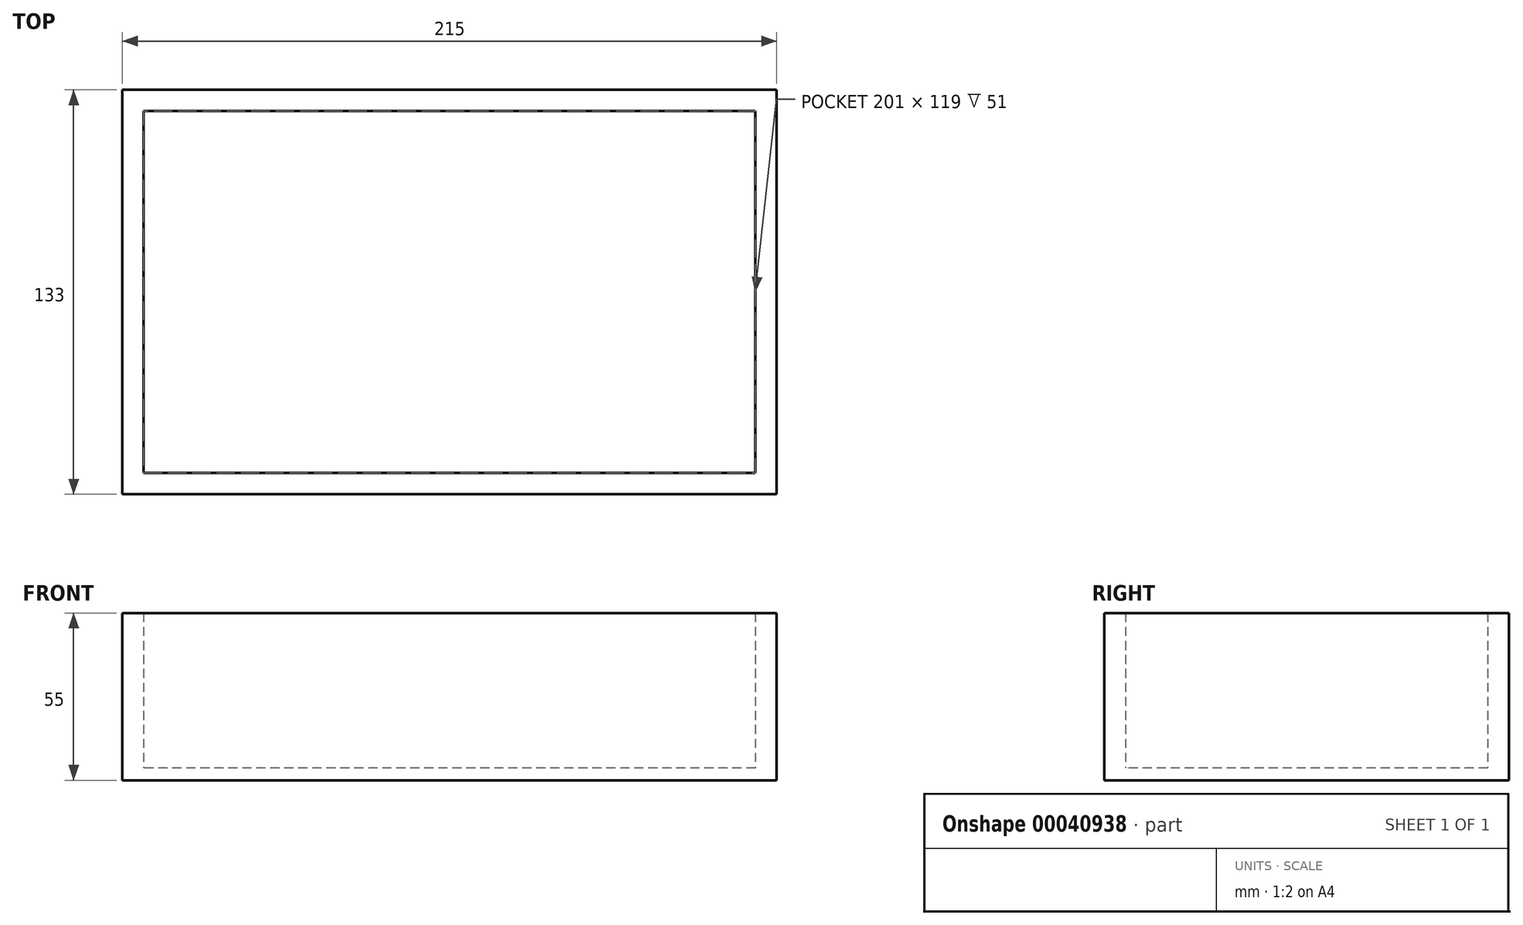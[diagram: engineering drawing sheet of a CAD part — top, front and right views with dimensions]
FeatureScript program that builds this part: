
annotation { "Feature Type Name" : "Feature", "Feature Type Description" : "" }
export const myFeature = defineFeature(function(context is Context, id is Id, definition is map)
    precondition{}
    {
        {
            var Q0;
            Q0=qCreatedBy(makeId("Top.planeOp"),FACE);
            var sketch = newSketch(context, id + "F0", { "sketchPlane" : qUnion([Q0])});
            skLineSegment(sketch, "E0.bottom", {"start": v(-99.18, 98.24) * mm, "end": v(115.82, 98.24) * mm});
            skLineSegment(sketch, "E0.top", {"start": v(-99.18, -34.76) * mm, "end": v(115.82, -34.76) * mm});
            skLineSegment(sketch, "E0.left", {"start": v(-99.18, 98.24) * mm, "end": v(-99.18, -34.76) * mm});
            skLineSegment(sketch, "E0.right", {"start": v(115.82, 98.24) * mm, "end": v(115.82, -34.76) * mm});
            skLineSegment(sketch, "E1.bottom", {"start": v(-99.18, -34.76) * mm, "end": v(-92.18, -34.76) * mm, "construction": true});
            skLineSegment(sketch, "E1.top", {"start": v(-99.18, -27.76) * mm, "end": v(-92.18, -27.76) * mm, "construction": true});
            skLineSegment(sketch, "E1.left", {"start": v(-99.18, -34.76) * mm, "end": v(-99.18, -27.76) * mm, "construction": true});
            skLineSegment(sketch, "E1.right", {"start": v(-92.18, -34.76) * mm, "end": v(-92.18, -27.76) * mm, "construction": true});
            skLineSegment(sketch, "E2.bottom", {"start": v(115.82, 98.24) * mm, "end": v(108.82, 98.24) * mm, "construction": true});
            skLineSegment(sketch, "E2.top", {"start": v(115.82, 91.24) * mm, "end": v(108.82, 91.24) * mm, "construction": true});
            skLineSegment(sketch, "E2.left", {"start": v(115.82, 98.24) * mm, "end": v(115.82, 91.24) * mm, "construction": true});
            skLineSegment(sketch, "E2.right", {"start": v(108.82, 98.24) * mm, "end": v(108.82, 91.24) * mm, "construction": true});
            skLineSegment(sketch, "E3.bottom", {"start": v(108.82, 91.24) * mm, "end": v(-92.18, 91.24) * mm});
            skLineSegment(sketch, "E3.top", {"start": v(108.82, -27.76) * mm, "end": v(-92.18, -27.76) * mm});
            skLineSegment(sketch, "E3.left", {"start": v(108.82, 91.24) * mm, "end": v(108.82, -27.76) * mm});
            skLineSegment(sketch, "E3.right", {"start": v(-92.18, 91.24) * mm, "end": v(-92.18, -27.76) * mm});
            skSolve(sketch);
        }
        {
            var Q0;
            Q0=makeQuery(id+"F0.imprint","IMPRINT",FACE,{"disambiguationData":[TD([[makeQuery(id+"F0.imprint","IMPRINT",EDGE,{"derivedFrom":sQuery(id+"F0.wireOp",EDGE,"E0.bottom")}),-1.0]])]});
            extrude(context, id + "F1", {"entities" : qUnion([Q0]), "depth" : 55 * mm});
        }
        {
            var Q0;
            Q0=makeQuery(id+"F0.imprint","IMPRINT",FACE,{"disambiguationData":[TD([[makeQuery(id+"F0.imprint","IMPRINT",EDGE,{"derivedFrom":sQuery(id+"F0.wireOp",EDGE,"E0.bottom")}),-1.0]])]});
            var Q1;
            Q1=makeQuery(id+"F0.imprint","IMPRINT",FACE,{"disambiguationData":[TD([[makeQuery(id+"F0.imprint","IMPRINT",EDGE,{"derivedFrom":sQuery(id+"F0.wireOp",EDGE,"E3.bottom")}),1.0]])]});
            extrude(context, id + "F2", {"entities" : qUnion([Q0, Q1]), "operationType" : NewBodyOperationType.ADD, "depth" : 4 * mm});
        }
    });
